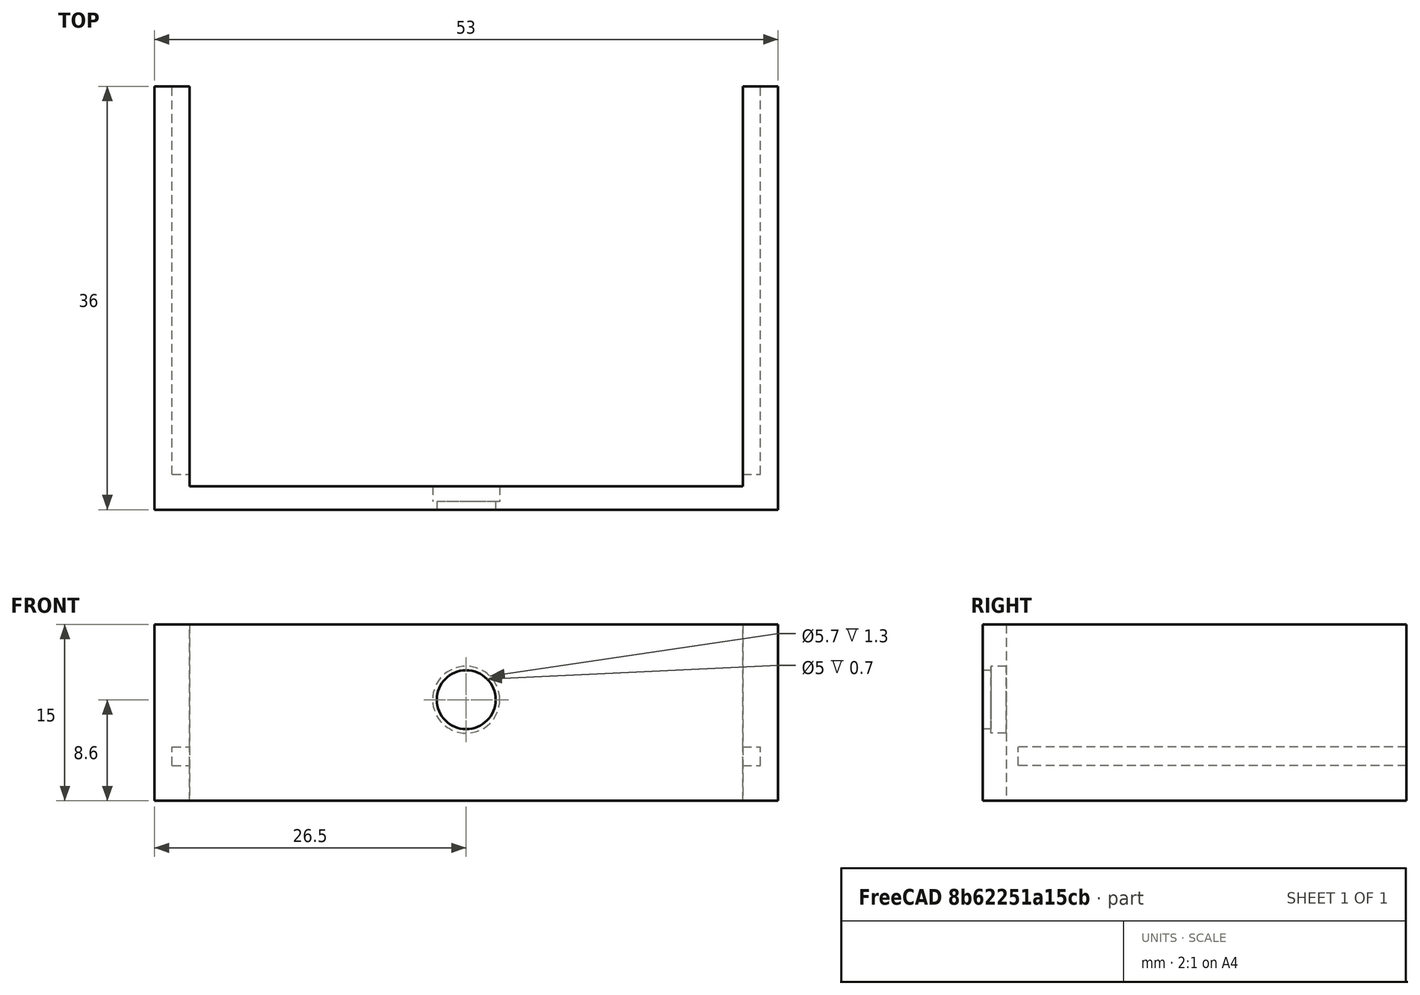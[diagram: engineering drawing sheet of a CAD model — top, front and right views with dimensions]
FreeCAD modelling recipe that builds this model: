
FCSTD DOCUMENT  (FreeCAD 0.15R4671 (Git))
Label: Sense_Beam_Tx
License: All rights reserved
LicenseURL: http://en.wikipedia.org/wiki/All_rights_reserved
objects: Part::Box×4, Part::Cylinder×2, Part::MultiFuse×2, Part::Cut×2, Drawing::FeatureViewPart×2, Drawing::FeatureViewPython×2, Drawing::FeaturePage×1
note: 10 computed .brp shape members not serialized (recipe doc carries the construction recipe); baked Part::Feature solids carry a one-line shape summary decoded from their .brp

FEATURE [Part::Box] Box001  label="side1"
  Height = 15
  Length = 3
  Width = 36
FEATURE [Part::Box] Box002  label="side2"
  Height = 15
  Length = 3
  Placement = pos=(50,0,0) rot=(0,0,1;0rad)
  Width = 36
FEATURE [Part::Box] Box003  label="Front"
  Height = 15
  Length = 53
  Width = 2
FEATURE [Part::Box] Box004  label="PCB"
  Height = 1.6
  Length = 50
  Placement = pos=(1.5,3,3) rot=(0,0,1;0rad)
  Width = 33
FEATURE [Part::Cylinder] Cylinder
  Angle = 360
  Height = 0.7
  Placement = pos=(26.5,0.7,8.6) rot=(1,0,0;1.5708rad)
  Radius = 2.5
FEATURE [Part::Cylinder] Cylinder001
  Angle = 360
  Height = 1.3
  Placement = pos=(26.5,2,8.6) rot=(1,0,0;1.5708rad)
  Radius = 2.85
FEATURE [Part::MultiFuse] Fusion001  label="LED"
  Shapes = -> [Cylinder,Cylinder001]
FEATURE [Part::Cut] Cut
  Base = -> Box003
  Tool = -> Fusion001
FEATURE [Part::MultiFuse] Fusion
  Shapes = -> [Cut,Box002,Box001]
FEATURE [Part::Cut] Cut001
  Base = -> Fusion
  Tool = -> Box004
FEATURE [Drawing::FeatureViewPart] Ortho  label="Ortho_0_0"
  Direction = (1,0,0)
  HiddenWidth = 0.15
  LineWidth = 0.35
  Rotation = -90
  Scale = 2
  ShowHiddenLines = false
  ShowSmoothLines = false
  Source = -> Cut001
  Tolerance = 0.05
  ViewResult = <g id="Ortho_0_0"\n   transform="rotate(-90,182,96.5) translate(182,96.5) scale(2,2)"\n  >\n<g   stroke="rgb(0, 0, 0)"\n   stroke-width="0.175"\n   stroke-linecap="butt"\n   stroke-linejoin="miter"\n   fill="none"\n   transform="scale(1,-1)"\n  >\n<path id= "1" d=" M 15 -2 L 15 -36 " />\n<path id= "2" d=" M 0 0 L 0 -2 " />\n<path d="M6.1,5.55112e-16 L6.11572,5.55112e-16  L6.16268,5.55112e-16  L6.24029,5.55112e-16  L6.34758,5.55112e-16  L6.48319,4.44089e-16  L6.64542,4.44089e-16  L6.83223,4.44089e-16  L7.04128,3.33067e-16  L7.26992,3.33067e-16  L7.51529,2.22045e-16  L7.7743,2.22045e-16  L8.0437,1.11022e-16  L8.32009,1.11022e-16  L8.6,0 " /><path id= "4" d=" M 15 -2 L 15 -36 " />\n<path id= "5" d=" M 0 -36 L 15 -36 " />\n<path id= "6" d=" M 0 -2 L 0 -36 " />\n<path id= "7" d=" M 15 0 L 15 -2 " />\n<path id= "8" d=" M 0 0 L 15 0 " />\n<path id= "9" d=" M 0 -2 L 15 -2 " />\n</g>\n</g>
  Visible = true
  X = 182
  Y = 96.5
FEATURE [Drawing::FeatureViewPart] Ortho001  label="Ortho_-1_0"
  Direction = (0,-1,0)
  HiddenWidth = 0.15
  LineWidth = 0.35
  Rotation = 90
  Scale = 2
  ShowHiddenLines = false
  ShowSmoothLines = false
  Source = -> Cut001
  Tolerance = 0.05
  ViewResult = <g id="Ortho_-1_0"\n   transform="rotate(90,43,96.5) translate(43,96.5) scale(2,2)"\n  >\n<g   stroke="rgb(0, 0, 0)"\n   stroke-width="0.175"\n   stroke-linecap="butt"\n   stroke-linejoin="miter"\n   fill="none"\n   transform="scale(1,-1)"\n  >\n<path id= "1" d=" M -15 0 L -15 3 " />\n<path id= "2" d=" M 0 0 L -15 0 " />\n<path id= "3" d=" M 0 0 L 0 3 " />\n<path id= "4" d=" M 0 3 L 0 50 " />\n<path id= "5" d=" M -15 3 L -15 50 " />\n<path id= "6" d=" M 0 3 L -15 3 " />\n<path id= "7" d=" M 0 50 L 0 53 " />\n<path id= "8" d=" M 0 50 L -15 50 " />\n<circle cx ="-8.6" cy ="26.5" r ="2.5" /><path id= "10" d=" M -15 50 L -15 53 " />\n<path id= "11" d=" M 0 53 L -15 53 " />\n</g>\n</g>
  Visible = true
  X = 43
  Y = 96.5
FEATURE [Drawing::FeatureViewPython] centerLines  # drawing view (typed FeaturePython)
  Rotation = 0
  ViewResult = <g transform="scale(2.000000,2.000000)" stroke="rgb(0,0,255)"  stroke-width="0.160000" > <path d="M 48.000000,39.650000 L 48.000000,41.150000 M 48.000000,42.150000 L 48.000000,44.853295 "/>\n<path d="M 48.000000,39.650000 L 49.500000,39.650000 M 50.500000,39.650000 L 53.500000,39.650000 M 54.500000,39.650000 L 55.804099,39.650000 "/>\n<path d="M 48.000000,39.650000 L 48.000000,38.150000 M 48.000000,37.150000 L 48.000000,34.150000 "/>\n<path d="M 48.000000,39.650000 L 46.500000,39.650000 M 45.500000,39.650000 L 42.500000,39.650000 M 41.500000,39.650000 L 40.000000,39.650000 "/> </g> 
  Visible = true
  X = 0
  Y = 0
  centerLine_color = rgb(0,0,255)
  centerLine_len_dash = 6
  centerLine_len_dot = 3
  centerLine_len_gap = 2
  centerLine_width = 0.32
  click1_x = 111.608
  click1_y = 89.7066
  click2_x = 78.0057
  click2_y = 66.9049
FEATURE [Drawing::FeatureViewPython] dim  # drawing view (typed FeaturePython)
  Rotation = 0
  ViewResult = <g> \n  <line x1="82.000000" y1="79.300000" x2="82.605995" y2="79.300000" style="stroke:rgb(0,0,255);stroke-width:0.50" />\n<line x1="45.000000" y1="96.500000" x2="82.605995" y2="96.500000" style="stroke:rgb(0,0,255);stroke-width:0.50" />\n<line x1="81.605995" y1="79.300000" x2="81.605995" y2="96.500000" style="stroke:rgb(0,0,255);stroke-width:0.50" /> \n  <polygon points="81.605995,96.500000 82.605995,93.500000 81.605995,92.500000 80.605995,93.500000" style="fill:rgb(0,0,255);stroke:rgb(0,0,255);stroke-width:0" /><polygon points="81.605995,79.300000 80.605995,82.300000 81.605995,83.300000 82.605995,82.300000" style="fill:rgb(0,0,255);stroke:rgb(0,0,255);stroke-width:0" /> \n  <text x="79.605995" y="87.900000" font-family="inherit" font-size="3.6" fill="rgb(0,0,255)" text-anchor="middle" transform="rotate(-90.000000 79.605995,87.900000)" >8.6</text> </g>
  Visible = true
  X = 0
  Y = 0
  arrowL1 = 3
  arrowL2 = 1
  arrowW = 2
  arrow_scheme = 0
  autoPlaceOffset = 2
  autoPlaceText = true
  click1_x = 81.606
  click1_y = 91.2067
  click2_x = 81.606
  click2_y = 91.2067
  comma_decimal_place = false
  dimension_line_overshoot = 1
  gap_datum_points = 2
  halfDimension_linear = false
  lineColor = rgb(0,0,255)
  strokeWidth = 0.5
  textFormat_linear = %(value)3.3f
  textRenderer_color = rgb(0,0,255)
  textRenderer_family = inherit
  textRenderer_size = 3.6
  unit_custom_scale = 1
  unit_scheme = 0
FEATURE [Drawing::FeaturePage] Page
  EditableTexts = Designed by Name | Date | Scale | Weight | Title | Subtitle | Drawing number | Sheet
  Group = -> [Ortho,Ortho001,centerLines,dim]
  Template = <path>
note: 1 file-system path scrubbed to <path> (originals preserved in the JSON sidecar)
